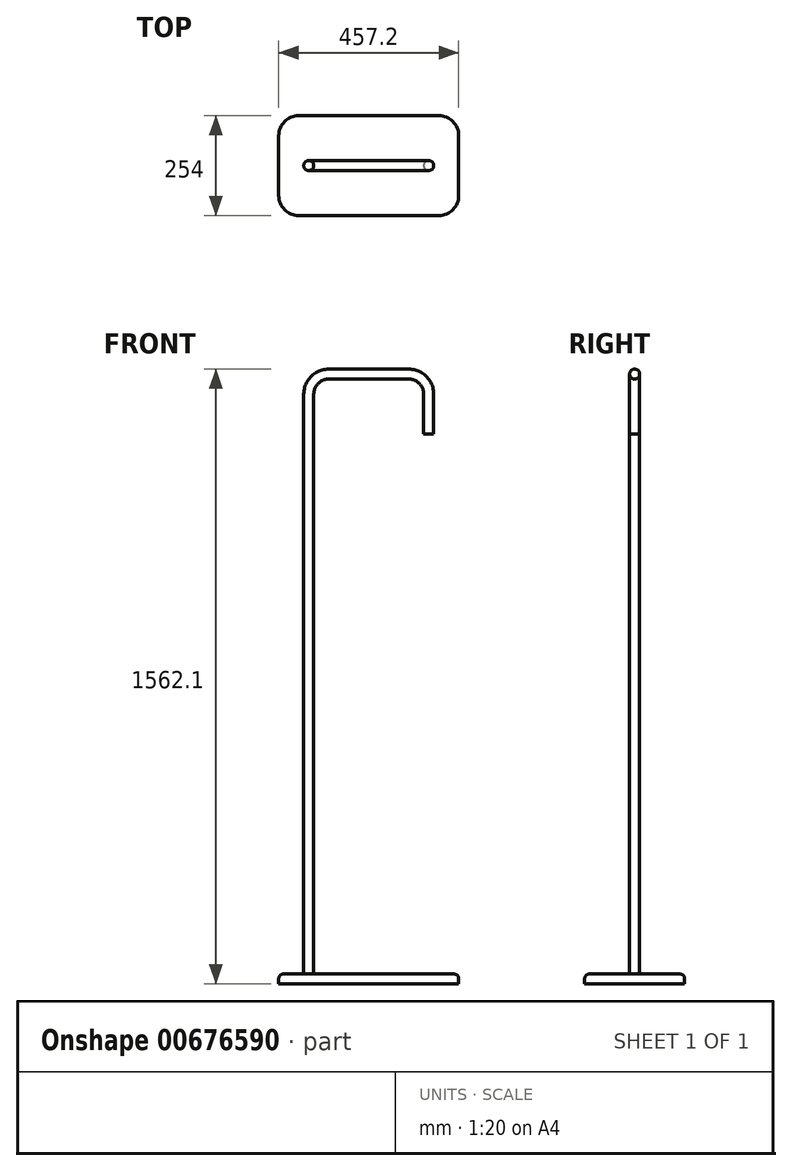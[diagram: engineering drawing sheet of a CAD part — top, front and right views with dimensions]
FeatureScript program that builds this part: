
annotation { "Feature Type Name" : "Feature", "Feature Type Description" : "" }
export const myFeature = defineFeature(function(context is Context, id is Id, definition is map)
    precondition{}
    {
        {
            var Q0;
            Q0=qCreatedBy(makeId("Top.planeOp"),FACE);
            var sketch = newSketch(context, id + "F0", { "sketchPlane" : qUnion([Q0])});
            skLineSegment(sketch, "E0.bottom", {"start": v(381, -127) * mm, "end": v(-76.2, -127) * mm});
            skLineSegment(sketch, "E0.top", {"start": v(381, 127) * mm, "end": v(-76.2, 127) * mm});
            skLineSegment(sketch, "E0.left", {"start": v(381, -127) * mm, "end": v(381, 127) * mm});
            skLineSegment(sketch, "E0.right", {"start": v(-76.2, -127) * mm, "end": v(-76.2, 127) * mm});
            skPoint(sketch, "E0.middle", {"position": v(152.4, 0) * mm});
            skSolve(sketch);
        }
        {
            var Q0;
            Q0=makeQuery(id+"F0.imprint","IMPRINT",FACE,{"disambiguationData":[TD([[makeQuery(id+"F0.imprint","IMPRINT",EDGE,{"derivedFrom":sQuery(id+"F0.wireOp",EDGE,"E0.bottom")}),-1.0]])]});
            extrude(context, id + "F1", {"entities" : qUnion([Q0]), "oppositeDirection" : true, "depth" : 25.4 * mm, "offsetDistance" : 25.4 * mm});
        }
        {
            var Q0;
            Q0=makeQuery(id+"F1.opExtrude","SWEPT_EDGE",EDGE,{"disambiguationData":[OSD([sQuery(id+"F0.wireOp",EDGE,"E0.bottom"),sQuery(id+"F0.wireOp",EDGE,"E0.right")])]});
            var Q1;
            Q1=makeQuery(id+"F1.opExtrude","SWEPT_EDGE",EDGE,{"disambiguationData":[OSD([sQuery(id+"F0.wireOp",EDGE,"E0.bottom"),sQuery(id+"F0.wireOp",EDGE,"E0.left")])]});
            var Q2;
            Q2=makeQuery(id+"F1.opExtrude","SWEPT_EDGE",EDGE,{"disambiguationData":[OSD([sQuery(id+"F0.wireOp",EDGE,"E0.top"),sQuery(id+"F0.wireOp",EDGE,"E0.left")])]});
            var Q3;
            Q3=makeQuery(id+"F1.opExtrude","SWEPT_EDGE",EDGE,{"disambiguationData":[OSD([sQuery(id+"F0.wireOp",EDGE,"E0.top"),sQuery(id+"F0.wireOp",EDGE,"E0.right")])]});
            fillet(context, id + "F2", {"entities" : qUnion([Q0, Q1, Q2, Q3]), "radius" : 50.8 * mm, "tangentPropagation" : true, "allowEdgeOverflow" : false});
        }
        {
            var Q0;
            Q0=makeQuery(id+"F1.opExtrude","CAP_EDGE",EDGE,{"disambiguationData":[OSD([sQuery(id+"F0.wireOp",EDGE,"E0.bottom")])],"isStart":true});
            fillet(context, id + "F3", {"entities" : qUnion([Q0]), "radius" : 12.7 * mm, "tangentPropagation" : true, "allowEdgeOverflow" : false});
        }
        {
            var Q0;
            Q0=makeQuery(id+"F1.opExtrude","CAP_FACE",FACE,{"disambiguationData":[OSD([sQuery(id+"F0.wireOp",EDGE,"E0.bottom"),sQuery(id+"F0.wireOp",EDGE,"E0.top"),sQuery(id+"F0.wireOp",EDGE,"E0.left"),sQuery(id+"F0.wireOp",EDGE,"E0.right")])],"isStart":true});
            var sketch = newSketch(context, id + "F4", { "sketchPlane" : qUnion([Q0])});
            skCircle(sketch, "E1", {"center": v(0, 0) * mm, "radius": 12.7 * mm});
            skSolve(sketch);
        }
        {
            var Q0;
            Q0=qCreatedBy(makeId("Front.planeOp"),FACE);
            var sketch = newSketch(context, id + "F5", { "sketchPlane" : qUnion([Q0])});
            skLineSegment(sketch, "E2", {"start": v(0, 0) * mm, "end": v(0, 1473.2) * mm});
            skLineSegment(sketch, "E3", {"start": v(50.8, 1524) * mm, "end": v(254, 1524) * mm});
            skLineSegment(sketch, "E4", {"start": v(304.8, 1473.2) * mm, "end": v(304.8, 1371.6) * mm});
            skPoint(sketch, "E5.visualSharp", {"position": v(0, 1524) * mm});
            skArc(sketch, "E5.filletArc", {"start": v(50.8, 1524) * mm, "mid": v(14.88, 1509.12) * mm, "end": v(0, 1473.2) * mm});
            skPoint(sketch, "E6.visualSharp", {"position": v(304.8, 1524) * mm});
            skArc(sketch, "E6.filletArc", {"start": v(304.8, 1473.2) * mm, "mid": v(289.92, 1509.12) * mm, "end": v(254, 1524) * mm});
            skSolve(sketch);
        }
        {
            var Q0;
            Q0 = qSketchRegion(id + "F4", true);
            var Q1;
            Q1 = qConstructionFilter(qBodyType(qCreatedBy(id + "F5" ,EDGE), BodyType.WIRE), ConstructionObject.NO);
            sweep(context, id + "F6", {"operationType" : NewBodyOperationType.ADD, "profiles" : qUnion([Q0]), "path" : qUnion([Q1])});
        }
    });
